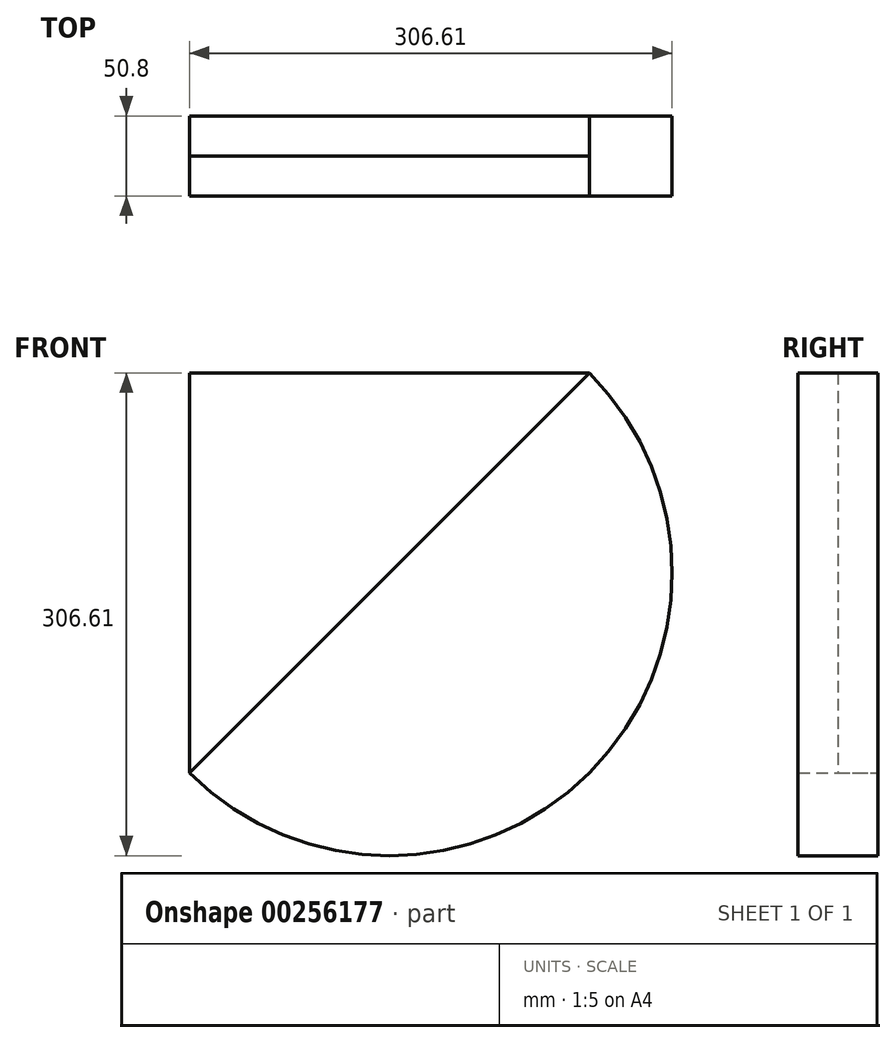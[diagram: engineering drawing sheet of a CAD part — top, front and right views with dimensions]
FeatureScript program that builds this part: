
annotation { "Feature Type Name" : "Feature", "Feature Type Description" : "" }
export const myFeature = defineFeature(function(context is Context, id is Id, definition is map)
    precondition{}
    {
        {
            var Q0;
            Q0=qCreatedBy(makeId("Front.planeOp"),FACE);
            var sketch = newSketch(context, id + "F0", { "sketchPlane" : qUnion([Q0])});
            skPoint(sketch, "E0.middle", {"position": v(0, 0) * mm});
            skLineSegment(sketch, "E1.bottom", {"start": v(-127, 127) * mm, "end": v(127, 127) * mm});
            skLineSegment(sketch, "E1.left", {"start": v(-127, 127) * mm, "end": v(-127, -127) * mm});
            skLineSegment(sketch, "E2", {"start": v(-127, -127) * mm, "end": v(127, 127) * mm});
            skArc(sketch, "E3", {"start": v(-127, -127) * mm, "mid": v(127, -127) * mm, "end": v(127, 127) * mm});
            skPoint(sketch, "E1.top.end.orphan", {"position": v(127, -127) * mm});
            skSolve(sketch);
        }
        {
            var Q0;
            Q0=makeQuery(id+"F0.imprint","IMPRINT",FACE,{"disambiguationData":[TD([[makeQuery(id+"F0.imprint","IMPRINT",EDGE,{"derivedFrom":sQuery(id+"F0.wireOp",EDGE,"E1.bottom")}),-1.0]])]});
            extrude(context, id + "F1", {"entities" : qUnion([Q0]), "depth" : 25.4 * mm});
        }
        {
            var Q0;
            Q0=makeQuery(id+"F0.imprint","IMPRINT",FACE,{"disambiguationData":[TD([[makeQuery(id+"F0.imprint","IMPRINT",EDGE,{"derivedFrom":sQuery(id+"F0.wireOp",EDGE,"E2")}),-1.0]])]});
            var Q1;
            Q1=sQuery(id+"F0.wireOp",EDGE,"E3");
            var Q2;
            Q2=sQuery(id+"F0.wireOp",EDGE,"E2");
            extrude(context, id + "F2", {"entities" : qUnion([Q0]), "surfaceEntities" : qUnion([Q1, Q2]), "depth" : 50.8 * mm});
        }
    });
